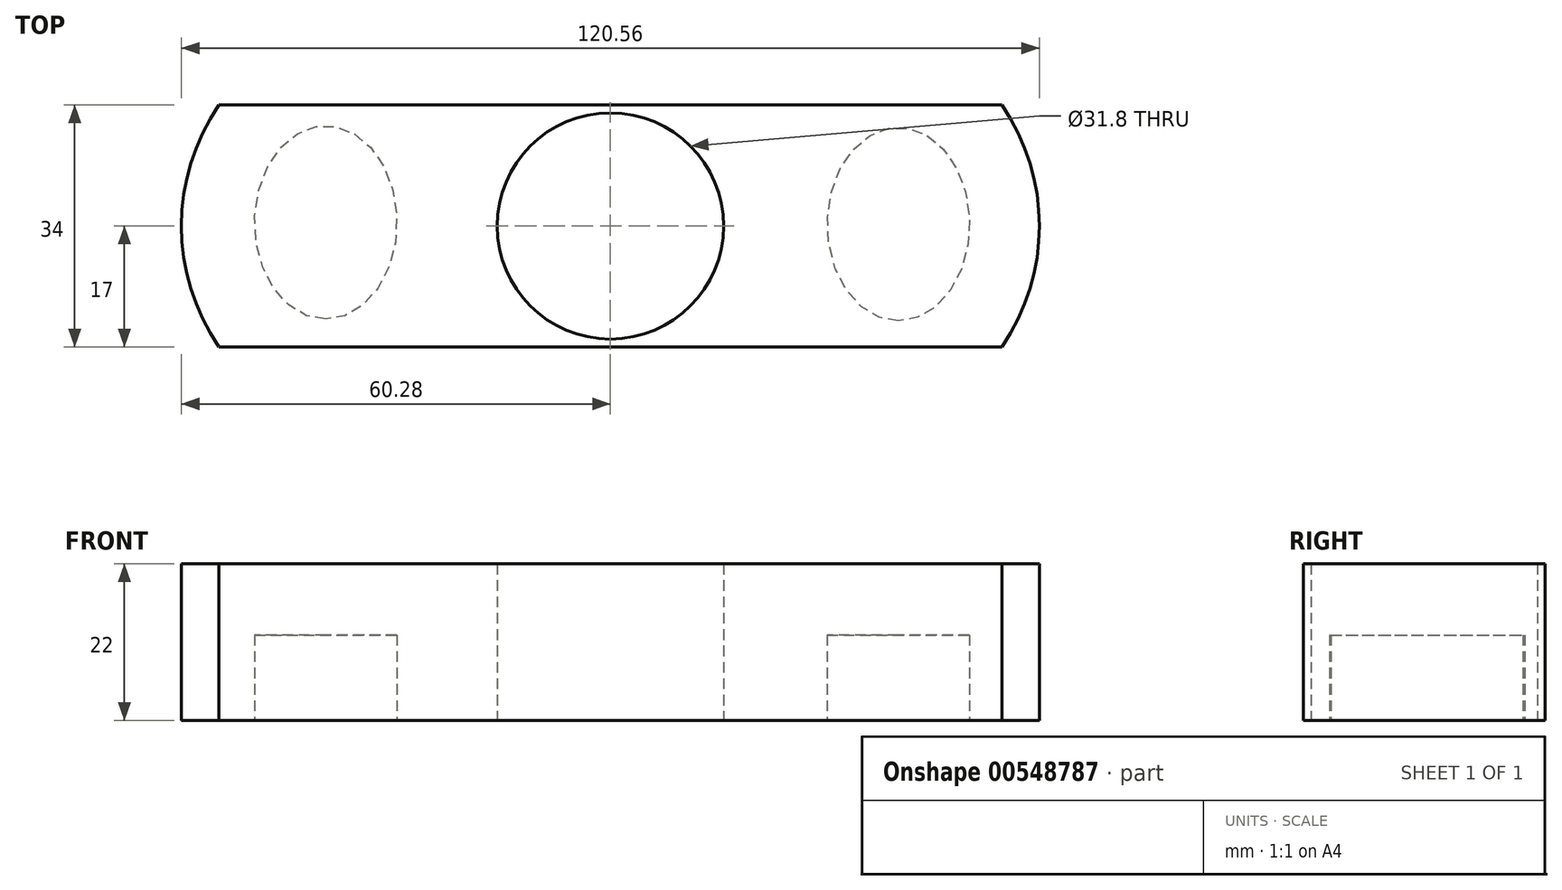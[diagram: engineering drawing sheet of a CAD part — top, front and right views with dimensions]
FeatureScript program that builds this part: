
annotation { "Feature Type Name" : "Feature", "Feature Type Description" : "" }
export const myFeature = defineFeature(function(context is Context, id is Id, definition is map)
    precondition{}
    {
        {
            var Q0;
            Q0=qCreatedBy(makeId("Top.planeOp"),FACE);
            var sketch = newSketch(context, id + "F0", { "sketchPlane" : qUnion([Q0])});
            skLineSegment(sketch, "E0", {"start": v(0, 0) * mm, "end": v(110, 0) * mm});
            skLineSegment(sketch, "E1", {"start": v(0, 34) * mm, "end": v(110, 34) * mm});
            skArc(sketch, "E2", {"start": v(0, 34) * mm, "mid": v(-5.28, 17) * mm, "end": v(0, 0) * mm});
            skArc(sketch, "E3", {"start": v(110, 0) * mm, "mid": v(115.28, 17) * mm, "end": v(110, 34) * mm});
            skPoint(sketch, "E4", {"position": v(110, 0) * mm});
            skPoint(sketch, "E5", {"position": v(55, 0) * mm});
            skPoint(sketch, "E6", {"position": v(55, 17) * mm});
            skCircle(sketch, "E7", {"center": v(55, 17) * mm, "radius": 15.9 * mm});
            skSolve(sketch);
        }
        {
            var Q0;
            Q0=makeQuery(id+"F0.imprint","IMPRINT",FACE,{"disambiguationData":[TD([[makeQuery(id+"F0.imprint","IMPRINT",EDGE,{"derivedFrom":sQuery(id+"F0.wireOp",EDGE,"E0")}),1.0]])]});
            extrude(context, id + "F1", {"entities" : qUnion([Q0]), "endBound" : BoundingType.SYMMETRIC, "depth" : 22 * mm, "offsetDistance" : 25 * mm});
        }
        {
            var Q0;
            Q0=makeQuery(id+"F1.opExtrude","CAP_FACE",FACE,{"disambiguationData":[OSD([sQuery(id+"F0.wireOp",EDGE,"E0"),sQuery(id+"F0.wireOp",EDGE,"E1"),sQuery(id+"F0.wireOp",EDGE,"E2"),sQuery(id+"F0.wireOp",EDGE,"E3"),sQuery(id+"F0.wireOp",EDGE,"E7")])],"isStart":true});
            var sketch = newSketch(context, id + "F2", { "sketchPlane" : qUnion([Q0])});
            skPoint(sketch, "E8", {"position": v(15, -17.5) * mm});
            skPoint(sketch, "E9", {"position": v(95, -17.5) * mm});
            skEllipse(sketch, "E10", {"center": v(15, -17.5) * mm, "majorRadius": 13.6 * mm, "minorRadius": 10 * mm, "majorAxis": v(0, 1)});
            skEllipse(sketch, "E11", {"center": v(95.48, -17.26) * mm, "majorRadius": 13.6 * mm, "minorRadius": 10 * mm, "majorAxis": v(0, 1)});
            skSolve(sketch);
        }
        {
            var Q0;
            Q0=makeQuery(id+"F2.imprint","IMPRINT",FACE,{"disambiguationData":[TD([[makeQuery(id+"F2.imprint","IMPRINT",EDGE,{"derivedFrom":sQuery(id+"F2.wireOp",EDGE,"E10")}),1.0]])]});
            var Q1;
            Q1=makeQuery(id+"F2.imprint","IMPRINT",FACE,{"disambiguationData":[TD([[makeQuery(id+"F2.imprint","IMPRINT",EDGE,{"derivedFrom":sQuery(id+"F2.wireOp",EDGE,"E11")}),1.0]])]});
            var Q2;
            Q2=sQuery(id+"F2.wireOp",EDGE,"E10");
            var Q3;
            Q3=sQuery(id+"F2.wireOp",EDGE,"E11");
            extrude(context, id + "F3", {"entities" : qUnion([Q0, Q1]), "operationType" : NewBodyOperationType.REMOVE, "surfaceEntities" : qUnion([Q2, Q3]), "oppositeDirection" : true, "depth" : 12 * mm, "offsetDistance" : 25 * mm});
        }
    });
